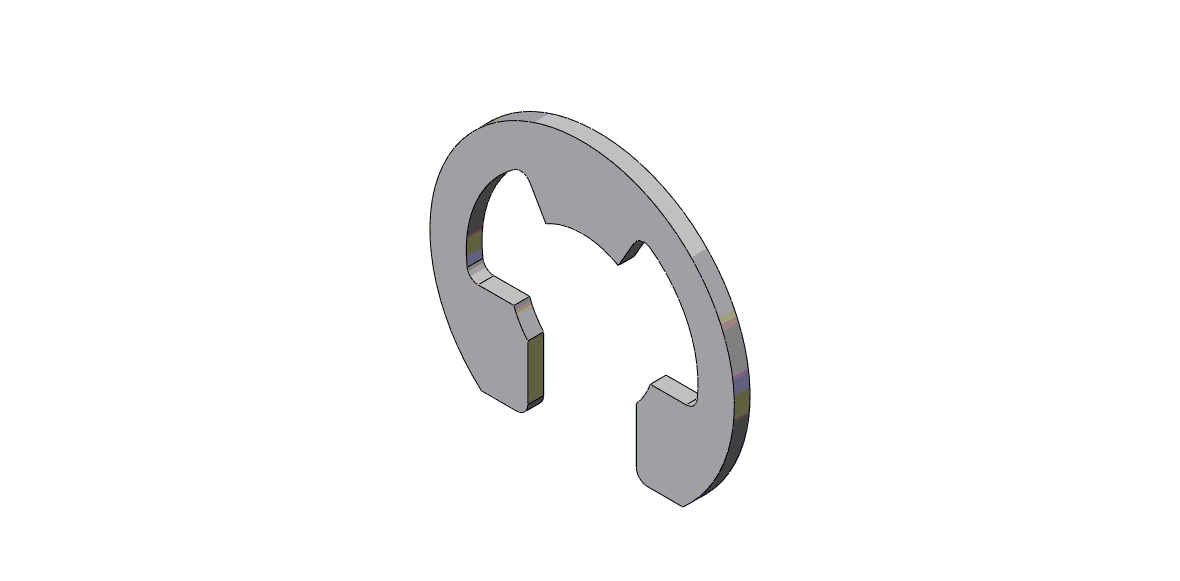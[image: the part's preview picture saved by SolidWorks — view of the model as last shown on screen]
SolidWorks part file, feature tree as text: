
SOLIDWORKS PART (.sldprt)
format: sldprt  version: not decoded by parser v0  size: 273,920 bytes
history: native  units: mm
features: sketch x2, material x1, extrude x1, fillet x1, revolve x1 (+13 scaffold rows collapsed)
feature tree (19):
  scaffold x13  (default folders/planes/origin — collapsed)
  material  "Plain Carbon Steel"
  sketch  "Sketch1"  dims[c1.OD=~95.467344mm c1.L=21.082mm c1.Df=~44.936653mm c1.D=9.779mm c1.D1=4.1148mm c1.D5=1.1938mm c2.D1=~7.833032mm c2.OD=20.574mm c2.D2=3.4671mm c3.D2=~60.241448deg c4.D2=2.3368mm c4.D3=~6.844632mm c4.D4=~0.839061mm c4.D5=~4.638511mm c5.D2=~27.72918mm c5.D3=~2.26822mm c5.D5=~0.509803mm c5.D4=~12.285631mm c6.D3=~12.285631mm c6.D2=~0.876627mm c7.D3=~12.285631mm c7.D4=~0.516565mm c8.D3=~7.33425mm c8.D2=~0.495924mm c9.D2=60.0deg c9.D4=~18.00225mm c9.D5=~1.629833mm]
  extrude  "Extrude1"  Depth=1.0668mm
  fillet  "Fillet1"  Radius=0.74676mm
  sketch  "Sketch3"  dims[c1.Ds=19.05mm c1.Dg=10.0584mm c1.W=1.1684mm c1.D1=5.3975mm c1.D2=11.684mm c1.D3=~0.855501mm c2.D3=45.0deg c2.D1=2.921mm c3.D3=~1.439371mm c4.D3=45.0deg c4.Ds=12.7mm]
  revolve  "Revolve2"  Angle=360deg
decode coverage: 5 of 5 modeling features carry decoded parameters
note: ~ marks probable driven/reference dimensions
note: suppression state not decoded; provenance and decode notes live in map.json
